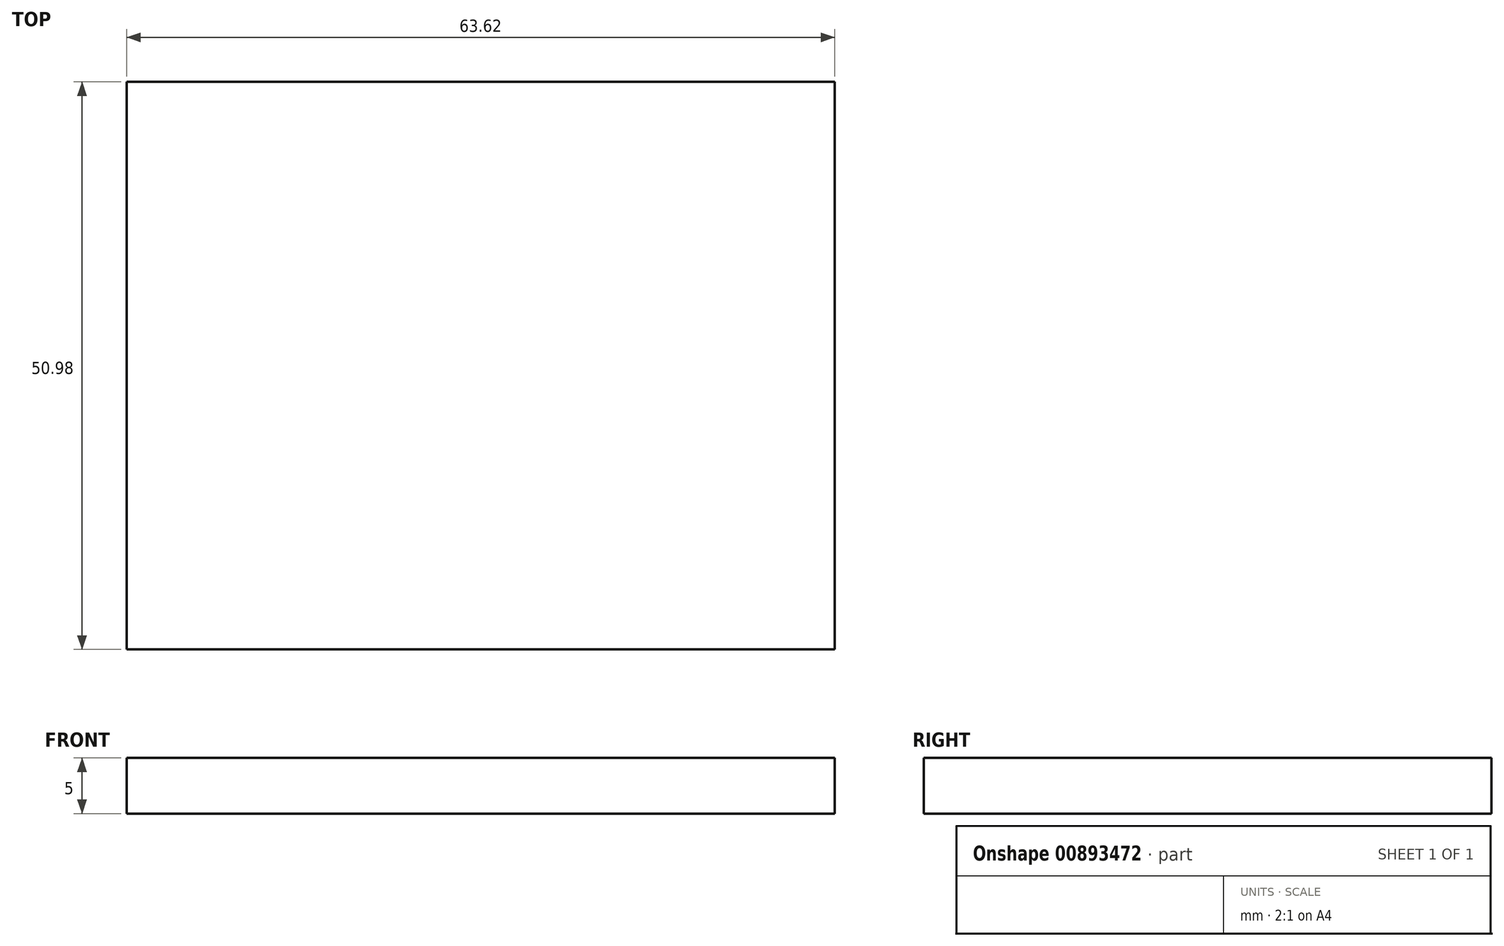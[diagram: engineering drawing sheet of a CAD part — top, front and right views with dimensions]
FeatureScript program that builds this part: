
annotation { "Feature Type Name" : "Feature", "Feature Type Description" : "" }
export const myFeature = defineFeature(function(context is Context, id is Id, definition is map)
    precondition{}
    {
        {
            var Q0;
            Q0=qCreatedBy(makeId("Top.planeOp"),FACE);
            var sketch = newSketch(context, id + "F0", { "sketchPlane" : qUnion([Q0])});
            skLineSegment(sketch, "E0.bottom", {"start": v(-31.8, 25.5) * mm, "end": v(31.8, 25.5) * mm});
            skLineSegment(sketch, "E0.top", {"start": v(-31.8, -25.5) * mm, "end": v(31.8, -25.5) * mm});
            skLineSegment(sketch, "E0.left", {"start": v(-31.8, 25.5) * mm, "end": v(-31.8, -25.5) * mm});
            skLineSegment(sketch, "E0.right", {"start": v(31.8, 25.5) * mm, "end": v(31.8, -25.5) * mm});
            skPoint(sketch, "E0.middle", {"position": v(0, 0) * mm});
            skSolve(sketch);
        }
        {
            var Q0;
            Q0=makeQuery(id+"F0.imprint","IMPRINT",FACE,{"disambiguationData":[TD([[makeQuery(id+"F0.imprint","IMPRINT",EDGE,{"derivedFrom":sQuery(id+"F0.wireOp",EDGE,"E0.bottom")}),-1.0]])]});
            extrude(context, id + "F1", {"entities" : qUnion([Q0]), "depth" : 5 * mm, "offsetDistance" : 25 * mm});
        }
    });
